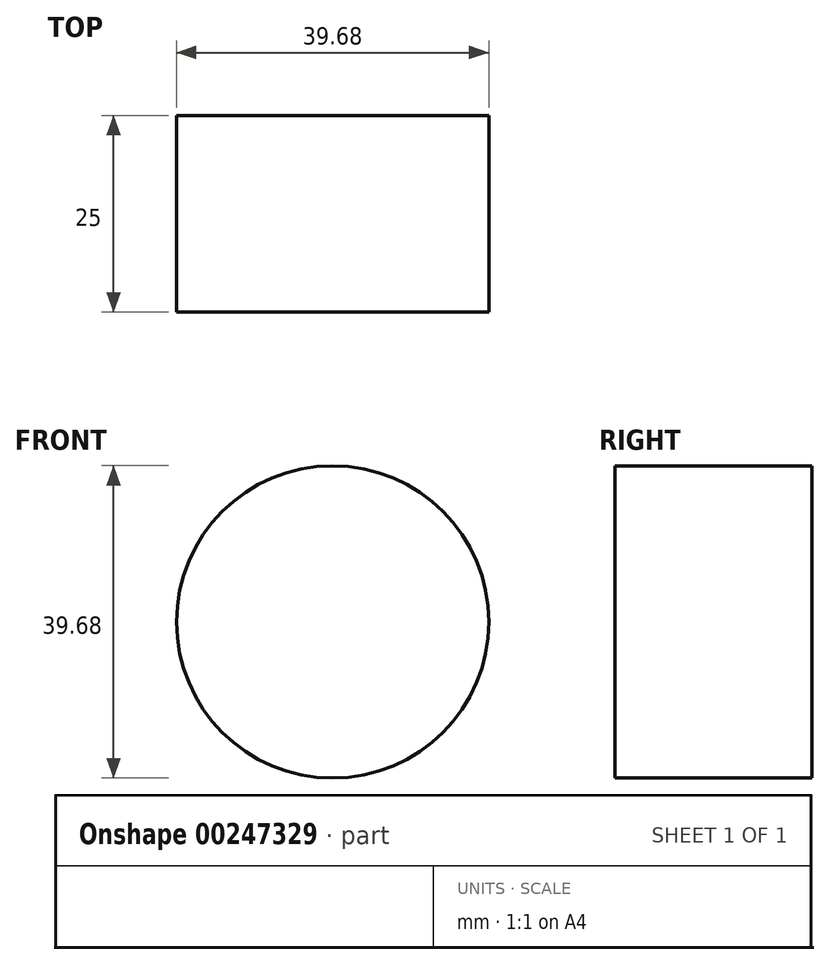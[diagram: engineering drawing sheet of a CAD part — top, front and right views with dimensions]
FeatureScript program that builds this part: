
annotation { "Feature Type Name" : "Feature", "Feature Type Description" : "" }
export const myFeature = defineFeature(function(context is Context, id is Id, definition is map)
    precondition{}
    {
        {
            var Q0;
            Q0=qCreatedBy(makeId("Front.planeOp"),FACE);
            var sketch = newSketch(context, id + "F0", { "sketchPlane" : qUnion([Q0])});
            skCircle(sketch, "E0", {"center": v(0, 0) * mm, "radius": 19.84 * mm});
            skSolve(sketch);
        }
        {
            var Q0;
            Q0=makeQuery(id+"F0.imprint","IMPRINT",FACE,{"disambiguationData":[TD([[makeQuery(id+"F0.imprint","IMPRINT",EDGE,{"derivedFrom":sQuery(id+"F0.wireOp",EDGE,"E0")}),1.0]])]});
            extrude(context, id + "F1", {"entities" : qUnion([Q0]), "depth" : 25 * mm});
        }
    });
